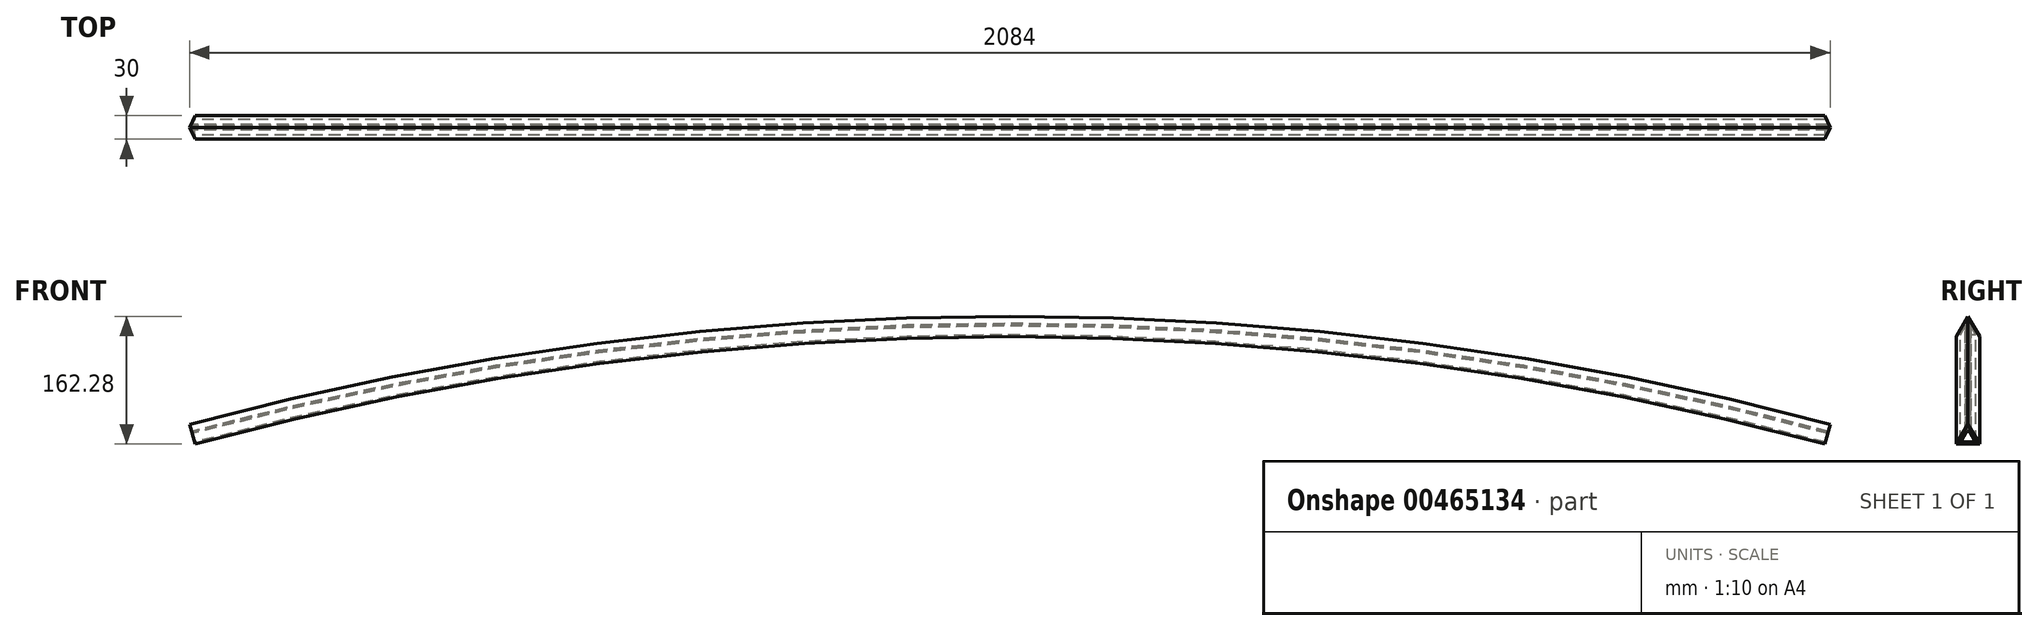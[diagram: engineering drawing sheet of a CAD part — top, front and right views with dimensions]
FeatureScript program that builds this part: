
annotation { "Feature Type Name" : "Feature", "Feature Type Description" : "" }
export const myFeature = defineFeature(function(context is Context, id is Id, definition is map)
    precondition{}
    {
        {
            var Q0;
            Q0=qCreatedBy(makeId("Right.planeOp"),FACE);
            var sketch = newSketch(context, id + "F0", { "sketchPlane" : qUnion([Q0])});
            skLineSegment(sketch, "E0", {"start": v(-15, 0) * mm, "end": v(15, 0) * mm});
            skLineSegment(sketch, "E1", {"start": v(15, 0) * mm, "end": v(0, 25.98) * mm});
            skLineSegment(sketch, "E2", {"start": v(0, 25.98) * mm, "end": v(-15, 0) * mm});
            skLineSegment(sketch, "E3", {"start": v(-10, 2.41) * mm, "end": v(10, 2.41) * mm});
            skLineSegment(sketch, "E4", {"start": v(0, 19.73) * mm, "end": v(-10, 2.41) * mm});
            skLineSegment(sketch, "E5", {"start": v(10, 2.41) * mm, "end": v(0, 19.73) * mm});
            skLineSegment(sketch, "E6", {"start": v(-10.95, -4000) * mm, "end": v(9.33, -4000) * mm});
            skLineSegment(sketch, "E7", {"start": v(0, 19.73) * mm, "end": v(0, 2.41) * mm});
            skLineSegment(sketch, "E8", {"start": v(0, 2.41) * mm, "end": v(0, 16.73) * mm});
            skLineSegment(sketch, "E9", {"start": v(0, 16.73) * mm, "end": v(2.05, 16.18) * mm});
            skLineSegment(sketch, "E10", {"start": v(2.05, 16.18) * mm, "end": v(0, 16.73) * mm});
            skLineSegment(sketch, "E11", {"start": v(-2.05, 16.18) * mm, "end": v(0, 16.73) * mm});
            skPoint(sketch, "E12", {"position": v(1.02, 16.46) * mm});
            skLineSegment(sketch, "E13", {"start": v(1.02, 16.46) * mm, "end": v(2.58, 15.26) * mm});
            skPoint(sketch, "E14", {"position": v(1.8, 15.86) * mm});
            skLineSegment(sketch, "E15", {"start": v(1.8, 15.86) * mm, "end": v(3.07, 14.41) * mm});
            skPoint(sketch, "E16", {"position": v(2.44, 15.14) * mm});
            skLineSegment(sketch, "E17", {"start": v(2.44, 15.14) * mm, "end": v(3.55, 13.58) * mm});
            skLineSegment(sketch, "E18.MirrorCS", {"start": v(-1.02, 16.46) * mm, "end": v(-2.58, 15.26) * mm});
            skLineSegment(sketch, "E19.MirrorCS", {"start": v(-1.8, 15.86) * mm, "end": v(-3.07, 14.41) * mm});
            skLineSegment(sketch, "E20.MirrorCS", {"start": v(-2.44, 15.14) * mm, "end": v(-3.55, 13.58) * mm});
            skSolve(sketch);
        }
        {
            var Q0;
            Q0=makeQuery(id+"F0.imprint","IMPRINT",FACE,{"disambiguationData":[TD([[makeQuery(id+"F0.imprint","IMPRINT",EDGE,{"derivedFrom":sQuery(id+"F0.wireOp",EDGE,"E0")}),1.0]])]});
            var Q1;
            {var subQ0=sQuery(id+"F0.wireOp",EDGE,"E7");Q1=makeQuery(id+"F0.imprint","IMPRINT",FACE,{"disambiguationData":[TD([[makeQuery(id+"F0.imprint","IMPRINT",EDGE,{"derivedFrom":subQ0}),1.0]])]});}
            var Q2;
            {var subQ0=sQuery(id+"F0.wireOp",EDGE,"E7");Q2=makeQuery(id+"F0.imprint","IMPRINT",FACE,{"disambiguationData":[TD([[makeQuery(id+"F0.imprint","IMPRINT",EDGE,{"derivedFrom":subQ0}),-1.0]])]});}
            var Q3;
            {var subQ0=sQuery(id+"F0.wireOp",EDGE,"E10");var subQ1=sQuery(id+"F0.wireOp",EDGE,"E5");var subQ2=makeQuery(id+"F0.imprint","INTERSECT",VERTEX,{"derivedFrom":[subQ1,subQ0]});Q3=makeQuery(id+"F0.imprint","IMPRINT",FACE,{"disambiguationData":[TD([[makeQuery(id+"F0.imprint","IMPRINT",EDGE,{"disambiguationData":[TD([[subQ2,1.0]])],"derivedFrom":subQ1}),1.0]])]});}
            var Q4;
            {var subQ0=sQuery(id+"F0.wireOp",EDGE,"E13");var subQ1=sQuery(id+"F0.wireOp",EDGE,"E5");var subQ2=makeQuery(id+"F0.imprint","INTERSECT",VERTEX,{"derivedFrom":[subQ1,subQ0]});Q4=makeQuery(id+"F0.imprint","IMPRINT",FACE,{"disambiguationData":[TD([[makeQuery(id+"F0.imprint","IMPRINT",EDGE,{"disambiguationData":[TD([[subQ2,1.0]])],"derivedFrom":subQ1}),1.0]])]});}
            var Q5;
            {var subQ3=sQuery(id+"F0.wireOp",EDGE,"E17");Q5=makeQuery(id+"F0.imprint","IMPRINT",FACE,{"disambiguationData":[TD([[makeQuery(id+"F0.imprint","IMPRINT",EDGE,{"derivedFrom":subQ3}),1.0]])]});}
            var Q6;
            {var subQ0=sQuery(id+"F0.wireOp",EDGE,"E19.MirrorCS");var subQ1=sQuery(id+"F0.wireOp",EDGE,"E4");var subQ2=makeQuery(id+"F0.imprint","INTERSECT",VERTEX,{"derivedFrom":[subQ1,subQ0]});Q6=makeQuery(id+"F0.imprint","IMPRINT",FACE,{"disambiguationData":[TD([[makeQuery(id+"F0.imprint","IMPRINT",EDGE,{"disambiguationData":[TD([[subQ2,1.0]])],"derivedFrom":subQ1}),1.0]])]});}
            var Q7;
            {var subQ3=sQuery(id+"F0.wireOp",EDGE,"E20.MirrorCS");Q7=makeQuery(id+"F0.imprint","IMPRINT",FACE,{"disambiguationData":[TD([[makeQuery(id+"F0.imprint","IMPRINT",EDGE,{"derivedFrom":subQ3}),-1.0]])]});}
            var Q8;
            {var subQ0=sQuery(id+"F0.wireOp",EDGE,"E11");var subQ1=sQuery(id+"F0.wireOp",EDGE,"E4");var subQ2=makeQuery(id+"F0.imprint","INTERSECT",VERTEX,{"derivedFrom":[subQ1,subQ0]});Q8=makeQuery(id+"F0.imprint","IMPRINT",FACE,{"disambiguationData":[TD([[makeQuery(id+"F0.imprint","IMPRINT",EDGE,{"disambiguationData":[TD([[subQ2,-1.0]])],"derivedFrom":subQ1}),1.0]])]});}
            var Q9;
            Q9=sQuery(id+"F0.wireOp",EDGE,"E6");
            revolve(context, id + "F1", {"entities" : qUnion([Q0, Q1, Q2, Q3, Q4, Q5, Q6, Q7, Q8]), "axis" : qUnion([Q9]), "revolveType" : RevolveType.SYMMETRIC, "angle" : 30 * degree});
        }
    });
